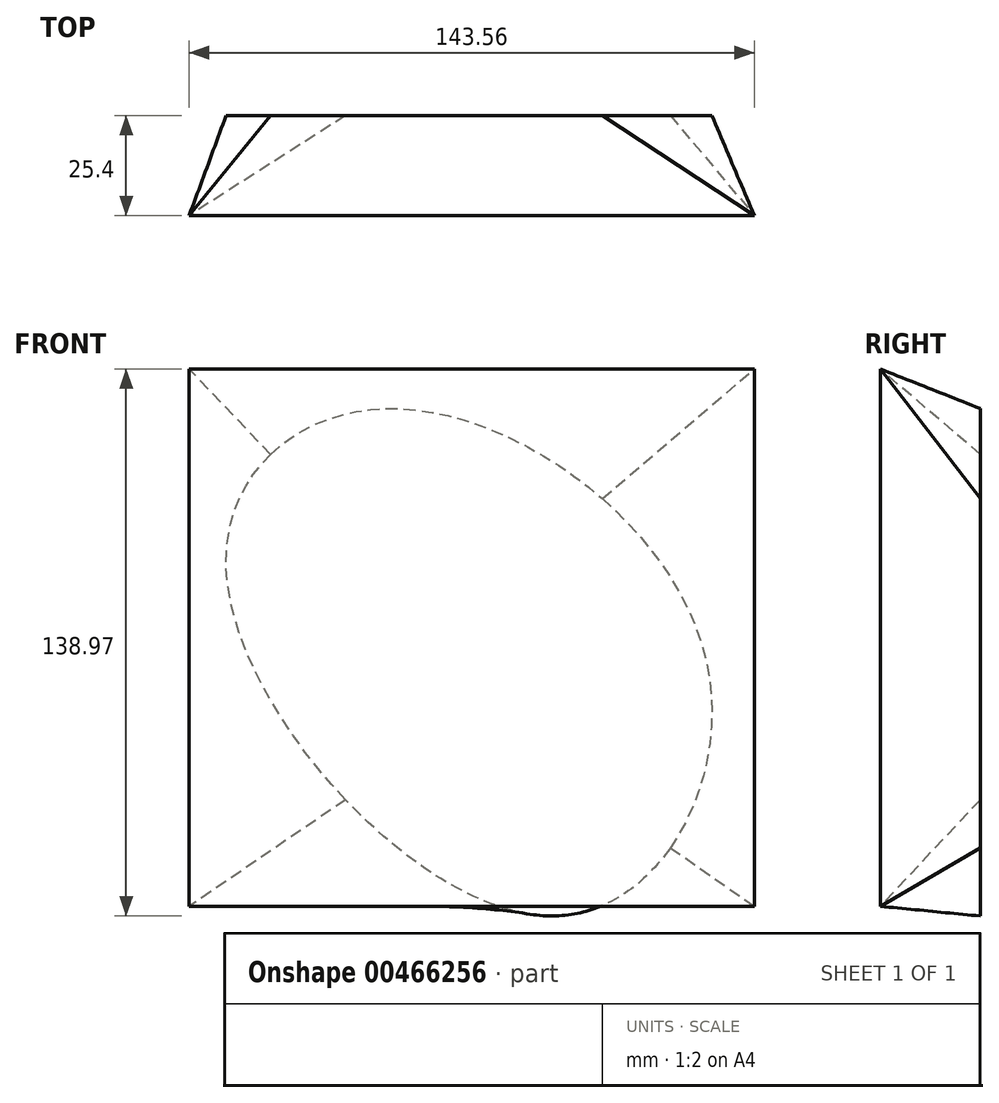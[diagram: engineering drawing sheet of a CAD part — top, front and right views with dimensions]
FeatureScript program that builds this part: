
annotation { "Feature Type Name" : "Feature", "Feature Type Description" : "" }
export const myFeature = defineFeature(function(context is Context, id is Id, definition is map)
    precondition{}
    {
        {
            var Q0;
            Q0=qCreatedBy(makeId("Front.planeOp"),FACE);
            var sketch = newSketch(context, id + "F0", { "sketchPlane" : qUnion([Q0])});
            skFitSpline(sketch, "E0", {"points": [v(-62.22, 18.97) * mm, v(-20.74, 62.03) * mm, v(59.8, -3.14) * mm, v(21.48, -66.9) * mm, v(-62.22, 18.97) * mm]});
            skSolve(sketch);
        }
        {
            var Q0;
            Q0=qCreatedBy(makeId("Front.planeOp"),FACE);
            cPlane(context, id + "F1", {"entities" : qUnion([Q0]), "cplaneType" : CPlaneType.OFFSET, "offset" : 25.4 * mm, "width" : 152.4 * mm, "height" : 152.4 * mm});
        }
        {
            var Q0;
            Q0=qCreatedBy(id+"F1.planeOp",FACE);
            var sketch = newSketch(context, id + "F2", { "sketchPlane" : qUnion([Q0])});
            skLineSegment(sketch, "E1.bottom", {"start": v(71.78, -64.46) * mm, "end": v(-71.78, -64.46) * mm});
            skLineSegment(sketch, "E1.top", {"start": v(71.78, 72.06) * mm, "end": v(-71.78, 72.06) * mm});
            skLineSegment(sketch, "E1.left", {"start": v(71.78, -64.46) * mm, "end": v(71.78, 72.06) * mm});
            skLineSegment(sketch, "E1.right", {"start": v(-71.78, -64.46) * mm, "end": v(-71.78, 72.06) * mm});
            skPoint(sketch, "E1.middle", {"position": v(0, 3.8) * mm});
            skSolve(sketch);
        }
        {
            var Q0;
            Q0 = qSketchRegion(id + "F0", true);
            var Q1;
            Q1 = qSketchRegion(id + "F2", true);
            loft(context, id + "F3", {"sheetProfilesArray" : [{ "sheetProfileEntities" : qUnion([Q0]) }, { "sheetProfileEntities" : qUnion([Q1]) }]});
        }
    });
